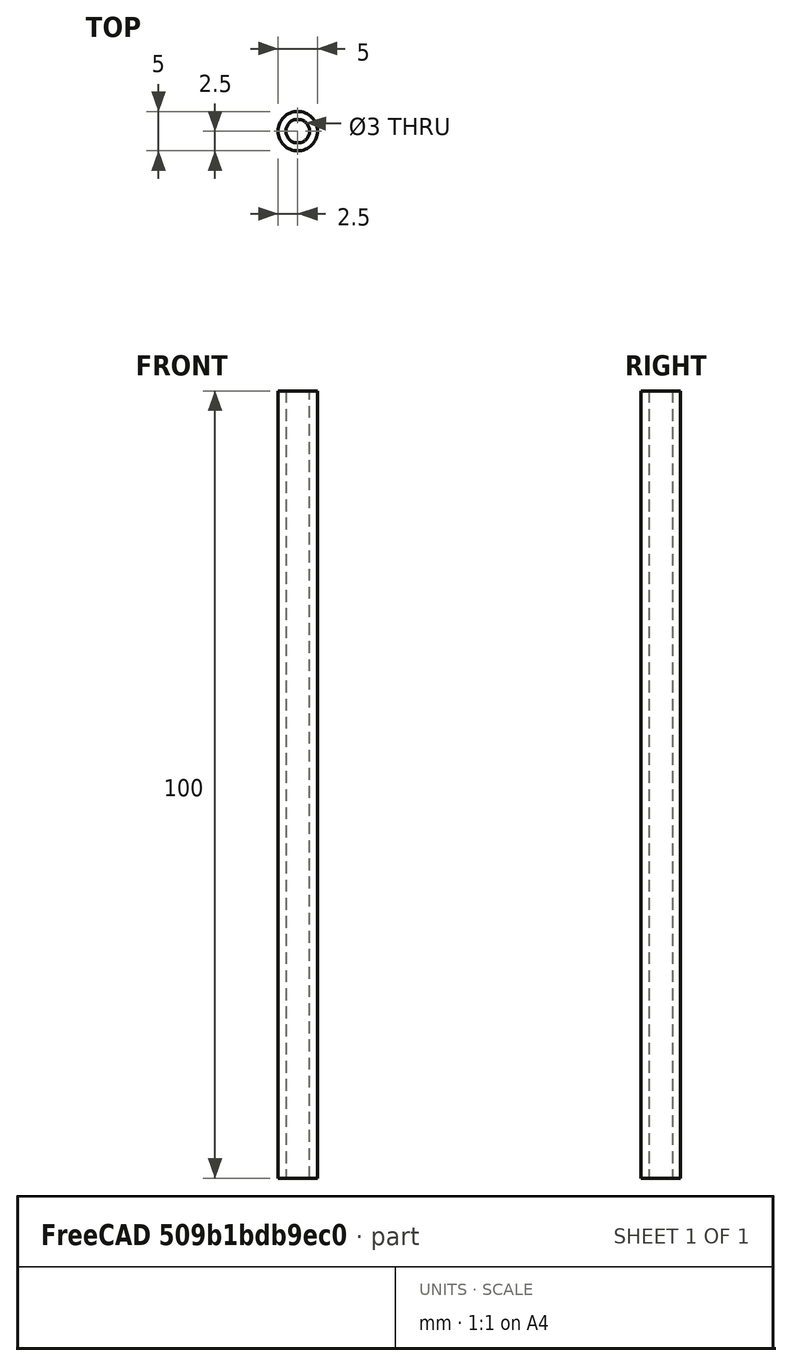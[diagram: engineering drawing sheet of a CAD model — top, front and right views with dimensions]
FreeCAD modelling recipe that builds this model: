
FCSTD DOCUMENT  (FreeCAD 1.0R39319 (Git))
Label: alluminium_rod
License: All rights reserved
LicenseURL: https://en.wikipedia.org/wiki/All_rights_reserved
objects: Sketcher::SketchObject×1, PartDesign::Pad×1, PartDesign::Body×1
note: 6 computed .brp shape members not serialized (recipe doc carries the construction recipe); baked Part::Feature solids carry a one-line shape summary decoded from their .brp

FEATURE [Sketcher::SketchObject] Sketch
  ArcFitTolerance = 1e-06
  AttachmentSupport = -> [XY_Plane]
  FullyConstrained = true
  MakeInternals = false
  MapMode = 5
  sketch-geometry (2):
    g0: Circle CenterX=0 CenterY=0 CenterZ=0 NormalX=0 NormalY=0 NormalZ=1 AngleXU=0 Radius=2.5
    g1: Circle CenterX=0 CenterY=0 CenterZ=0 NormalX=0 NormalY=0 NormalZ=1 AngleXU=0 Radius=1.5
  constraints (4):
    c: Diameter(g0) = 5
    c: Coincident(g0,g-1)
    c: Diameter(g1) = 3
    c: Coincident(g1,g0)
FEATURE [PartDesign::Pad] Pad
  Direction = (0,0,1)
  Length = 100
  Length2 = 10
  Profile = -> Sketch
  ReferenceAxis = -> Sketch [N_Axis]
  Refine = true
  Suppressed = false
  Type = 0
FEATURE [PartDesign::Body] Body
  AllowCompound = false
  Group = -> [Sketch,Pad]
  Origin = -> Origin
  Tip = -> Pad
